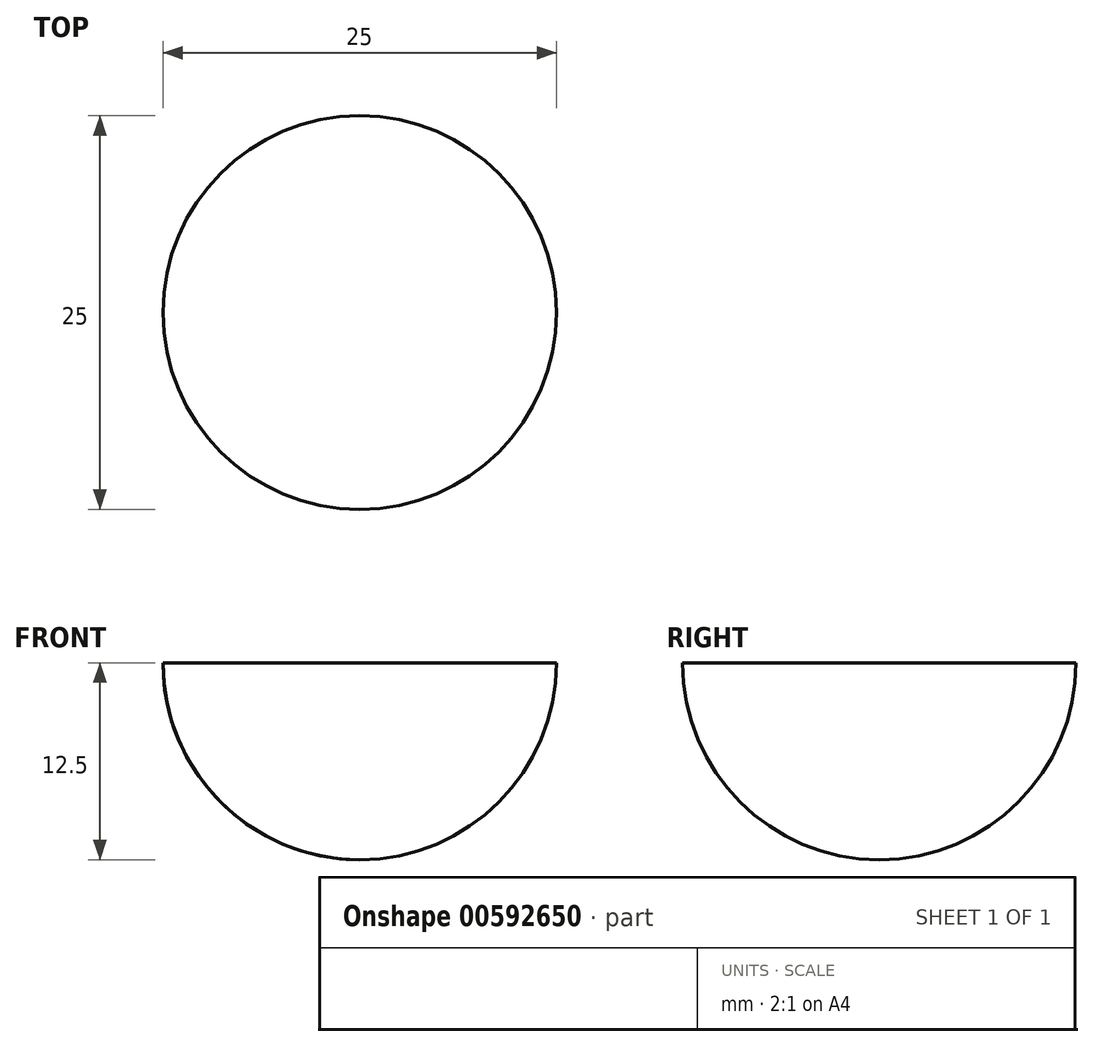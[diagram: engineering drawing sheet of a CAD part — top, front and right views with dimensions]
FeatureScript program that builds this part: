
annotation { "Feature Type Name" : "Feature", "Feature Type Description" : "" }
export const myFeature = defineFeature(function(context is Context, id is Id, definition is map)
    precondition{}
    {
        {
            var Q0;
            Q0=qCreatedBy(makeId("Front.planeOp"),FACE);
            var sketch = newSketch(context, id + "F0", { "sketchPlane" : qUnion([Q0])});
            skLineSegment(sketch, "E0", {"start": v(-12.5, 0) * mm, "end": v(0, 0) * mm});
            skArc(sketch, "E1", {"start": v(-12.5, 0) * mm, "mid": v(-8.84, -8.84) * mm, "end": v(0, -12.5) * mm});
            skLineSegment(sketch, "E2", {"start": v(0, 0) * mm, "end": v(0, -12.5) * mm});
            skSolve(sketch);
        }
        {
            var Q0;
            Q0=makeQuery(id+"F0.imprint","IMPRINT",FACE,{"disambiguationData":[TD([[makeQuery(id+"F0.imprint","IMPRINT",EDGE,{"derivedFrom":sQuery(id+"F0.wireOp",EDGE,"E0")}),-1.0]])]});
            var Q1;
            Q1=sQuery(id+"F0.wireOp",EDGE,"E2");
            revolve(context, id + "F1", {"entities" : qUnion([Q0]), "axis" : qUnion([Q1]), "revolveType" : RevolveType.FULL});
        }
    });
